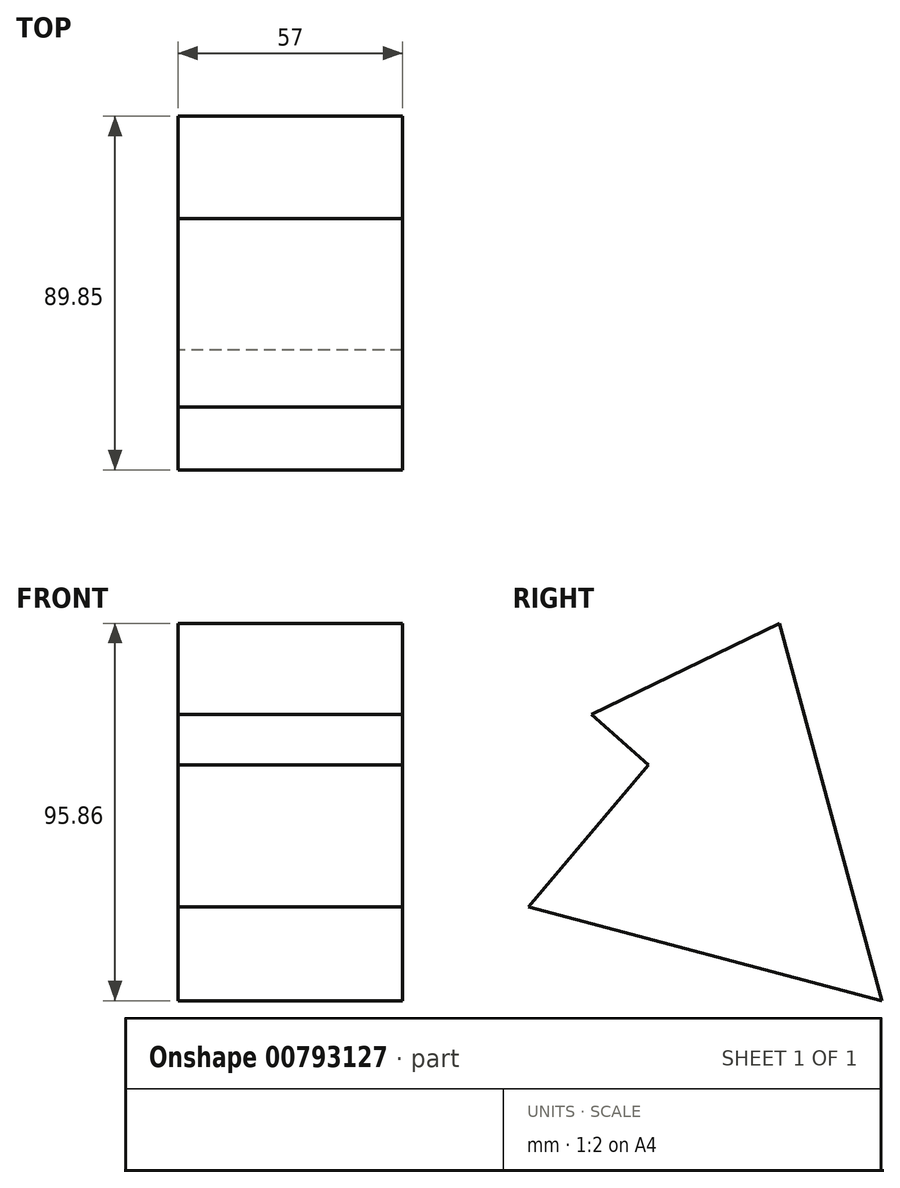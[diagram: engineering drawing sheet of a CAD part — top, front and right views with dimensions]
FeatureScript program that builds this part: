
annotation { "Feature Type Name" : "Feature", "Feature Type Description" : "" }
export const myFeature = defineFeature(function(context is Context, id is Id, definition is map)
    precondition{}
    {
        {
            var Q0;
            Q0=qCreatedBy(makeId("Right.planeOp"),FACE);
            var sketch = newSketch(context, id + "F0", { "sketchPlane" : qUnion([Q0])});
            skLineSegment(sketch, "E0", {"start": v(-30.75, 28.6) * mm, "end": v(17.08, 51.8) * mm});
            skLineSegment(sketch, "E1", {"start": v(17.08, 51.8) * mm, "end": v(43.12, -44.06) * mm});
            skLineSegment(sketch, "E2", {"start": v(43.12, -44.06) * mm, "end": v(-46.73, -20.26) * mm});
            skLineSegment(sketch, "E3", {"start": v(-46.73, -20.26) * mm, "end": v(-16.24, 15.9) * mm});
            skLineSegment(sketch, "E4", {"start": v(-16.24, 15.9) * mm, "end": v(-30.75, 28.6) * mm});
            skSolve(sketch);
        }
        {
            var Q0;
            Q0=makeQuery(id+"F0.imprint","IMPRINT",FACE,{"disambiguationData":[TD([[makeQuery(id+"F0.imprint","IMPRINT",EDGE,{"derivedFrom":sQuery(id+"F0.wireOp",EDGE,"E0")}),-1.0]])]});
            extrude(context, id + "F1", {"entities" : qUnion([Q0]), "depth" : 57 * mm, "offsetDistance" : 25 * mm});
        }
    });
